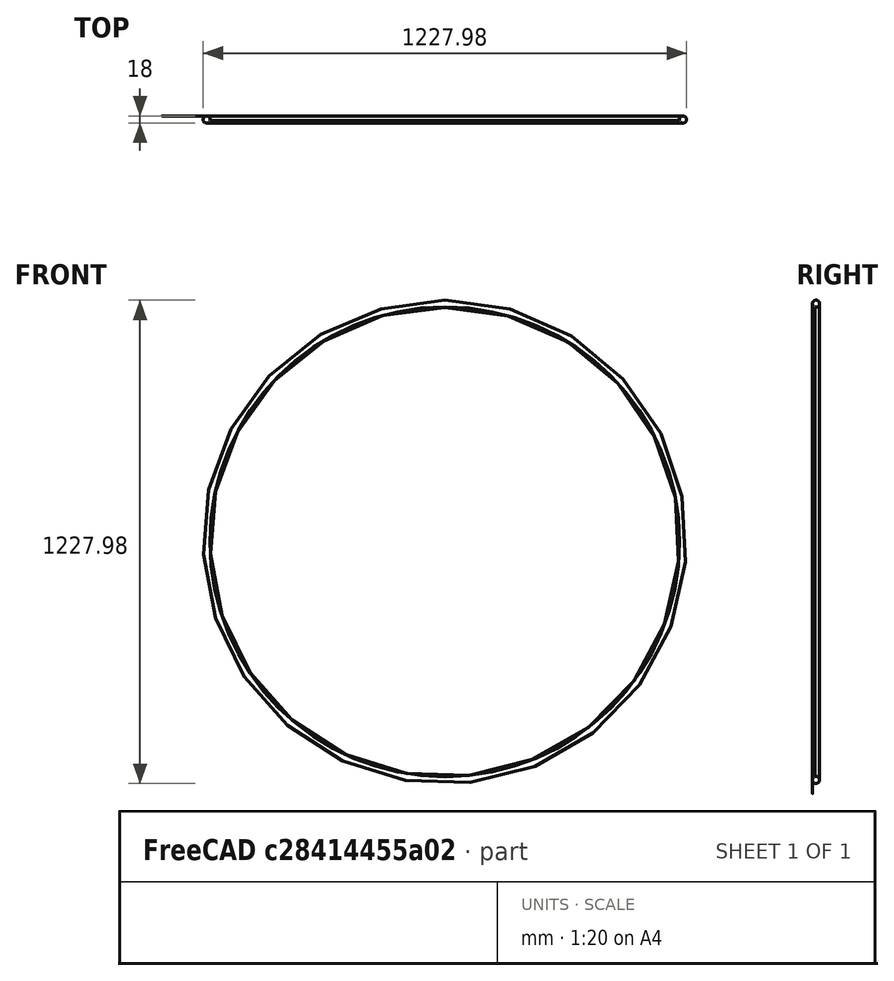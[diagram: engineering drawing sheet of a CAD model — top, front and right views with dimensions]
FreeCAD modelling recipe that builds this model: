
FCSTD DOCUMENT  (FreeCAD 0.18R16131 (Git))
Label: dish_with_rim_180cm_large_dish
License: All rights reserved
LicenseURL: http://en.wikipedia.org/wiki/All_rights_reserved
objects: Sketcher::SketchObject×1, PartDesign::Revolution×1, PartDesign::Body×1, App::Part×1
note: 4 computed .brp shape members not serialized (recipe doc carries the construction recipe); baked Part::Feature solids carry a one-line shape summary decoded from their .brp

FEATURE [Sketcher::SketchObject] Sketch
  MapMode = 5
  Placement = pos=(0,0,0) rot=(0.57735,0.57735,0.57735;2.0944rad)
  Support = -> [YZ_Plane001]
  expr: Constraints[19] = Constraints.thickness
  sketch-geometry (13):
    g0: GeomPoint X=-723.214 Y=0 Z=0
    g1: ArcOfParabola CenterX=0 CenterY=0 CenterZ=0 NormalX=0 NormalY=0 NormalZ=1 Focal=723.214 AngleXU=-3.14159 StartAngle=-900 EndAngle=0
    g2: GeomPoint X=-723.214 Y=0 Z=0
    g3: LineSegment [constr] StartX=0 StartY=0 StartZ=0 EndX=-723.214 EndY=0 EndZ=0
    g4: Circle [constr] CenterX=-272.358 CenterY=904.755 CenterZ=0 NormalX=0 NormalY=0 NormalZ=1 AngleXU=0 Radius=9
    g5: GeomPoint X=-280 Y=900 Z=0
    g6: ArcOfParabola CenterX=2 CenterY=0 CenterZ=0 NormalX=0 NormalY=0 NormalZ=1 Focal=723.214 AngleXU=3.14159 StartAngle=-896.432 EndAngle=0
    g7: GeomPoint X=-721.214 Y=0 Z=0
    g8: LineSegment [constr] StartX=2 StartY=0 StartZ=0 EndX=-721.214 EndY=0 EndZ=0
    g9: LineSegment StartX=0 StartY=0 StartZ=0 EndX=2 EndY=0 EndZ=0
    g10: GeomPoint X=-275.785 Y=896.432 Z=0
    g11: GeomPoint X=-275.785 Y=896.432 Z=0
    g12: ArcOfCircle CenterX=-272.358 CenterY=904.755 CenterZ=0 NormalX=0 NormalY=0 NormalZ=1 AngleXU=0 Radius=9 StartAngle=4.32187 EndAngle=9.98138
  constraints (30):
    c: PointOnObject(g0,g-1)
    c: InternalAlignment(g2,g1)
    c: Coincident(g2,g3)
    c: Coincident(g1,g3)
    c: Coincident(g2,g0)
    c: Coincident(g1,g-1)
    c: DistanceX(g0,g1) = 723.214
    c: DistanceY(g1,g1) = 900
    c: Horizontal(g1,g1)
    c: PointOnObject(g5,g4)
    c: Tangent(g1,g4,g5) = -1.5708
    c: Coincident(g5,g1)
    c: Diameter(g4) = 18
    c: PointOnObject(g6,g-1)
    c: InternalAlignment(g7,g6)
    c: Coincident(g7,g8)
    c: Coincident(g6,g8)
    c: PointOnObject(g7,g3)
    c: DistanceX(g1,g6) = 2  'thickness'
    c: DistanceX(g0,g7) = 2
    c: Horizontal(g6,g6)
    c: Coincident(g9,g1)
    c: Coincident(g9,g6)
    c: Coincident(g10,g11)
    c: Coincident(g10,g6)
    c: Coincident(g12,g4)
    c: Coincident(g12,g1)
    c: Coincident(g12,g6)
    c: DistanceX(g1,g1) = 280
    c: Distance(g1,g0) = 1003.21
FEATURE [PartDesign::Revolution] Revolution
  Angle = 360
  Axis = (3e-16,1,-2e-16)
  Base = (0,0,0)
  Placement = pos=(0,0,0) rot=(0.57735,0.57735,0.57735;2.0944rad)
  Profile = -> Sketch
  ReferenceAxis = -> Sketch [H_Axis]
FEATURE [PartDesign::Body] Body  label="DishWithRim"
  Group = -> [Sketch,Revolution]
  Origin = -> Origin001
  Tip = -> Revolution
FEATURE [App::Part] Part
  Group = -> [Body]
  Origin = -> Origin
